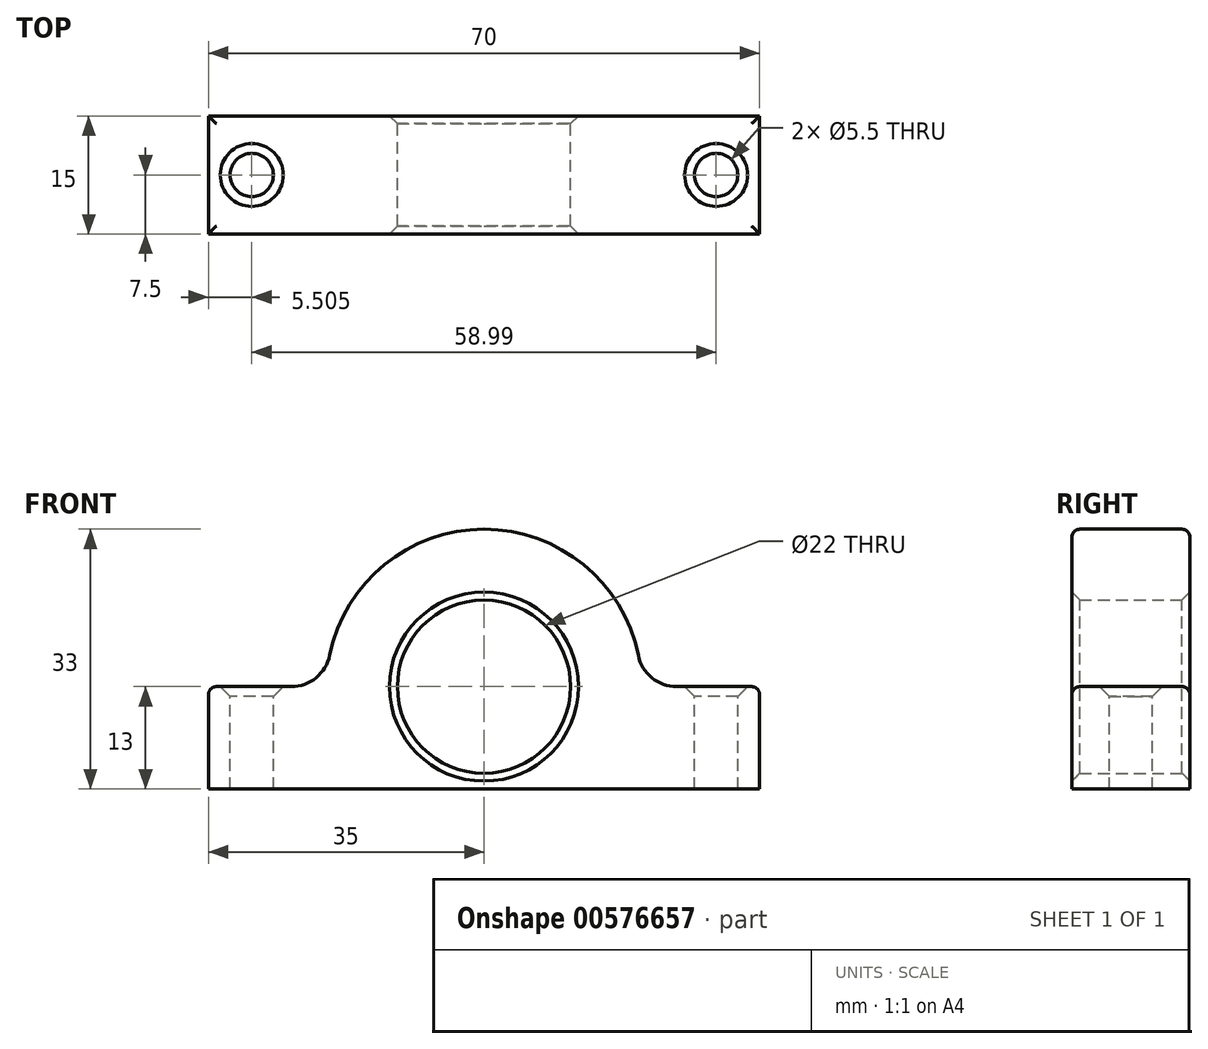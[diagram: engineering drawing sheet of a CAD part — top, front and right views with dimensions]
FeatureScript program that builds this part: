
annotation { "Feature Type Name" : "Feature", "Feature Type Description" : "" }
export const myFeature = defineFeature(function(context is Context, id is Id, definition is map)
    precondition{}
    {
        {
            var Q0;
            Q0=qCreatedBy(makeId("Front.planeOp"),FACE);
            var sketch = newSketch(context, id + "F0", { "sketchPlane" : qUnion([Q0])});
            skCircle(sketch, "E0", {"center": v(0, 0) * mm, "radius": 11 * mm});
            skArc(sketch, "E1", {"start": v(19.6, 4) * mm, "mid": v(0, 20) * mm, "end": v(-19.6, 4) * mm});
            skLineSegment(sketch, "E2", {"start": v(24.5, 0) * mm, "end": v(35, 0) * mm});
            skLineSegment(sketch, "E3", {"start": v(35, 0) * mm, "end": v(35, -13) * mm});
            skLineSegment(sketch, "E4", {"start": v(35, -13) * mm, "end": v(-35, -13) * mm});
            skLineSegment(sketch, "E5", {"start": v(-35, -13) * mm, "end": v(-35, 0) * mm});
            skLineSegment(sketch, "E6", {"start": v(-35, 0) * mm, "end": v(-24.5, 0) * mm});
            skPoint(sketch, "E7.visualSharp", {"position": v(20, 0) * mm});
            skArc(sketch, "E7.filletArc", {"start": v(19.6, 4) * mm, "mid": v(21.33, 1.13) * mm, "end": v(24.5, 0) * mm});
            skPoint(sketch, "E8.visualSharp", {"position": v(-20, 0) * mm});
            skArc(sketch, "E8.filletArc", {"start": v(-24.5, 0) * mm, "mid": v(-21.33, 1.13) * mm, "end": v(-19.6, 4) * mm});
            skSolve(sketch);
        }
        {
            var Q0;
            Q0 = qSketchRegion(id + "F0", true);
            extrude(context, id + "F1", {"entities" : qUnion([Q0]), "depth" : 15 * mm, "offsetDistance" : 25 * mm});
        }
        {
            var Q0;
            Q0=makeQuery(id+"F1.opExtrude","SWEPT_FACE",FACE,{"disambiguationData":[OSD([sQuery(id+"F0.wireOp",EDGE,"E2")])]});
            var sketch = newSketch(context, id + "F2", { "sketchPlane" : qUnion([Q0])});
            skLineSegment(sketch, "E9", {"start": v(29.5, -7.5) * mm, "end": v(29.5, -22.5) * mm});
            skLineSegment(sketch, "E10.MirrorCS", {"start": v(-29.5, -7.5) * mm, "end": v(-29.5, -22.5) * mm});
            skSolve(sketch);
        }
        {
            var Q0;
            Q0=sQuery(id+"F2.wireOp",VERTEX,"E10.MirrorCS.start");
            var Q1;
            Q1=sQuery(id+"F2.wireOp",VERTEX,"E10.MirrorCS.end");
            var Q2;
            Q2=sQuery(id+"F2.wireOp",VERTEX,"E9.start");
            var Q3;
            Q3=sQuery(id+"F2.wireOp",VERTEX,"E9.end");
            var Q4;
            Q4=makeQuery(id+"F1.opExtrude","SWEPT_BODY",BODY,{"disambiguationData":[OSD([sQuery(id+"F0.wireOp",EDGE,"E0"),sQuery(id+"F0.wireOp",EDGE,"E1"),sQuery(id+"F0.wireOp",EDGE,"E2"),sQuery(id+"F0.wireOp",EDGE,"E3"),sQuery(id+"F0.wireOp",EDGE,"E4"),sQuery(id+"F0.wireOp",EDGE,"E5"),sQuery(id+"F0.wireOp",EDGE,"E6"),sQuery(id+"F0.wireOp",EDGE,"E7.filletArc"),sQuery(id+"F0.wireOp",EDGE,"E8.filletArc")])]});
            hole(context, id + "F3", {"style" : HoleStyle.C_SINK, "endStyle" : HoleEndStyle.THROUGH, "holeDiameter" : 5.5 * mm, "cSinkDiameter" : 8 * mm, "cSinkAngle" : 90 * degree, "isTappedThrough" : true, "tappedDepth" : 12 * mm, "tapClearance" : 3, "locations" : qUnion([Q0, Q1, Q2, Q3]), "scope" : qUnion([Q4])});
        }
        {
            var Q0;
            Q0=makeQuery(id+"F1.opExtrude","CAP_EDGE",EDGE,{"disambiguationData":[OSD([sQuery(id+"F0.wireOp",EDGE,"E0")])],"isStart":false});
            var Q1;
            Q1=makeQuery(id+"F1.opExtrude","CAP_EDGE",EDGE,{"disambiguationData":[OSD([sQuery(id+"F0.wireOp",EDGE,"E0")])],"isStart":true});
            chamfer(context, id + "F4", {"entities" : qUnion([Q0, Q1]), "width" : 1 * mm, "tangentPropagation" : true});
        }
        {
            var Q0;
            Q0=makeQuery(id+"F1.opExtrude","CAP_EDGE",EDGE,{"disambiguationData":[OSD([sQuery(id+"F0.wireOp",EDGE,"E1")])],"isStart":true});
            var Q1;
            Q1=makeQuery(id+"F1.opExtrude","CAP_EDGE",EDGE,{"disambiguationData":[OSD([sQuery(id+"F0.wireOp",EDGE,"E1")])],"isStart":false});
            var Q2;
            Q2=makeQuery(id+"F1.opExtrude","SWEPT_EDGE",EDGE,{"disambiguationData":[OSD([sQuery(id+"F0.wireOp",EDGE,"E2"),sQuery(id+"F0.wireOp",EDGE,"E3")])]});
            var Q3;
            Q3=makeQuery(id+"F1.opExtrude","SWEPT_EDGE",EDGE,{"disambiguationData":[OSD([sQuery(id+"F0.wireOp",EDGE,"E5"),sQuery(id+"F0.wireOp",EDGE,"E6")])]});
            fillet(context, id + "F5", {"entities" : qUnion([Q0, Q1, Q2, Q3]), "radius" : 1 * mm, "tangentPropagation" : true, "allowEdgeOverflow" : false});
        }
    });
